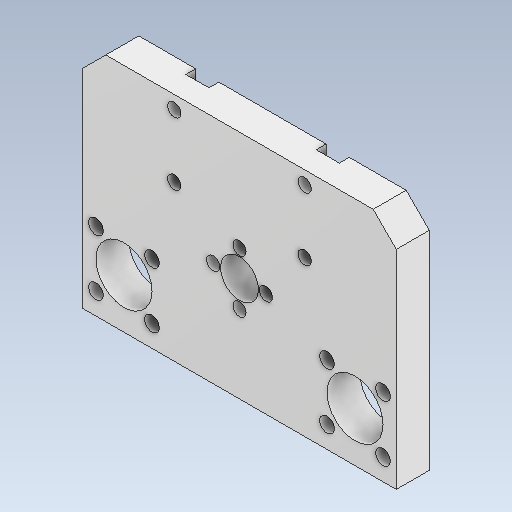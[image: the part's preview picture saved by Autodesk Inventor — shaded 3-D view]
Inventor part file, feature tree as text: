
AUTODESK INVENTOR PART (.ipt)
format: ipt  version: 2020 (Build 240168000, 168)  size: 249,344 bytes
history: native  units: mm
features: extrude x4, sketch x4, other x2, projected_geometry x2, hole x1, mirror x1, chamfer x1, reference x1
ambient origin geometry x8: Origin, YZ Plane, XZ Plane, XY Plane, X Axis, Y Axis, Z Axis, Center Point
bodies: Solid1 (feature_tree)
feature tree (16):
  extrude  "Extrusion1"  Depth=70.0mm
  extrude  "Extrusion2"  TaperAngle=0.0deg  [1 undecoded]
  extrude  "Extrusion3"  Depth=11.5mm
  hole  "Hole1"  [1 undecoded]
  extrude  "Extrusion4"  TaperAngle=0.0deg  [1 undecoded]
  mirror  "Mirror1"
  chamfer  "Chamfer1"  Distance=40.0mm Angle=360.0deg
  sketch  "Sketch1"  dims[d0=95.0mm d1=70.0mm]
  sketch  "Sketch2"  dims[d2=10.0mm d3=0.0mm d8=0.0mm d9=0.0mm]
  reference  "Reference1"
  sketch  "Sketch5"  dims[d10=31.597875mm d12=11.5mm]
  sketch  "Sketch6"  dims[d13=4.0mm d14=8.0mm d15=0.0mm d16=0.0mm d17=40.0mm d19=360.0deg d21=15.0mm d22=12.5mm d23=17.0mm d26=4.5mm d27=16.970563mm d28=16.970563mm d29=27.75mm d30=4.0mm d31=4.0mm d32=19.0mm d33=4.0mm d34=6.0mm d35=7.0mm d36=3.0mm d37=90.0deg d38=8.0mm d39=20.594885mm d40=10.0mm d41=0.0mm d42=7.0mm d43=2.0mm d44=45.0deg]
  other  "0008-10-10 Injectomat Standard.iam"
  other  "Body Syringe:1"
  projected_geometry  "Project Cut Edges1"
  projected_geometry  "Project Cut Edges2"
note: 3 required parameter values undecoded (feature->parameter linkage not recoverable at this tier; creation-order binding heuristic only, values carry confidence <= 0.55)
